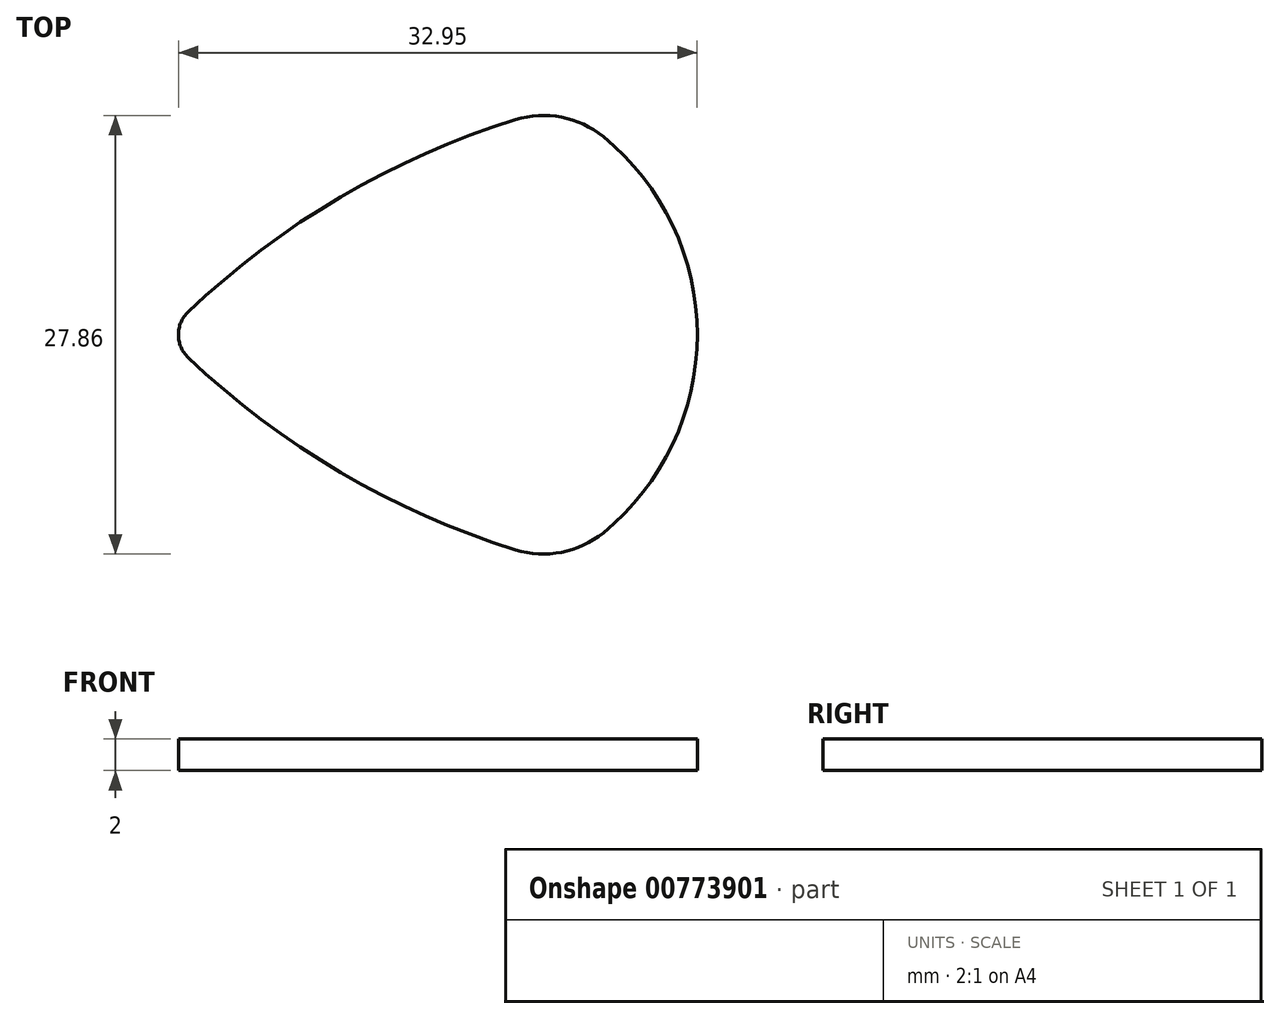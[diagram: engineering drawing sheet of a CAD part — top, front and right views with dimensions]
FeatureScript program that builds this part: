
annotation { "Feature Type Name" : "Feature", "Feature Type Description" : "" }
export const myFeature = defineFeature(function(context is Context, id is Id, definition is map)
    precondition{}
    {
        {
            var Q0;
            Q0=qCreatedBy(makeId("Top.planeOp"),FACE);
            var sketch = newSketch(context, id + "F0", { "sketchPlane" : qUnion([Q0])});
            skCircle(sketch, "E0.cCircle", {"center": v(0, 0) * mm, "radius": 8.33 * mm, "construction": true});
            skLineSegment(sketch, "E0.0", {"start": v(8.33, 14.43) * mm, "end": v(8.33, -14.43) * mm});
            skLineSegment(sketch, "E0.1", {"start": v(8.33, -14.43) * mm, "end": v(-16.67, 0) * mm});
            skLineSegment(sketch, "E0.2", {"start": v(-16.67, 0) * mm, "end": v(8.33, 14.43) * mm});
            skPoint(sketch, "E0.0.midPoint", {"position": v(8.33, 0) * mm});
            skPoint(sketch, "E1.visualSharp", {"position": v(-16.67, 0) * mm});
            skPoint(sketch, "E2.visualSharp", {"position": v(8.33, -14.43) * mm});
            skPoint(sketch, "E3.visualSharp", {"position": v(8.33, 14.43) * mm});
            skArc(sketch, "E4", {"start": v(-15.2, -1.45) * mm, "mid": v(-5.5, -8.75) * mm, "end": v(5.59, -13.66) * mm});
            skArc(sketch, "E5", {"start": v(5.59, 13.66) * mm, "mid": v(-5.5, 8.75) * mm, "end": v(-15.2, 1.45) * mm});
            skArc(sketch, "E6.filletArc", {"start": v(-15.2, 1.45) * mm, "mid": v(-15.82, 0) * mm, "end": v(-15.2, -1.45) * mm});
            skArc(sketch, "E7", {"start": v(11.16, -12.58) * mm, "mid": v(17.13, 0) * mm, "end": v(11.16, 12.58) * mm});
            skArc(sketch, "E8.filletArc", {"start": v(11.16, 12.58) * mm, "mid": v(8.51, 13.82) * mm, "end": v(5.59, 13.66) * mm});
            skArc(sketch, "E9.filletArc", {"start": v(5.59, -13.66) * mm, "mid": v(8.51, -13.82) * mm, "end": v(11.16, -12.58) * mm});
            skSolve(sketch);
        }
        {
            var Q0;
            {var subQ5=sQuery(id+"F0.wireOp",EDGE,"E7");Q0=makeQuery(id+"F0.imprint","IMPRINT",FACE,{"disambiguationData":[TD([[makeQuery(id+"F0.imprint","IMPRINT",EDGE,{"derivedFrom":subQ5}),1.0]])]});}
            var Q1;
            {var subQ5=sQuery(id+"F0.wireOp",EDGE,"E5");Q1=makeQuery(id+"F0.imprint","IMPRINT",FACE,{"disambiguationData":[TD([[makeQuery(id+"F0.imprint","IMPRINT",EDGE,{"derivedFrom":subQ5}),1.0]])]});}
            var Q2;
            {var subQ5=sQuery(id+"F0.wireOp",EDGE,"E8.filletArc");var subQ6=sQuery(id+"F0.wireOp",EDGE,"E0.0");var subQ7=makeQuery(id+"F0.imprint","INTERSECT",VERTEX,{"derivedFrom":[subQ6,subQ5]});Q2=makeQuery(id+"F0.imprint","IMPRINT",FACE,{"disambiguationData":[TD([[makeQuery(id+"F0.imprint","IMPRINT",EDGE,{"disambiguationData":[TD([[subQ7,-1.0]])],"derivedFrom":subQ6}),-1.0]])]});}
            var Q3;
            {var subQ5=sQuery(id+"F0.wireOp",EDGE,"E4");Q3=makeQuery(id+"F0.imprint","IMPRINT",FACE,{"disambiguationData":[TD([[makeQuery(id+"F0.imprint","IMPRINT",EDGE,{"derivedFrom":subQ5}),1.0]])]});}
            extrude(context, id + "F1", {"entities" : qUnion([Q0, Q1, Q2, Q3]), "depth" : 2 * mm, "offsetDistance" : 25 * mm});
        }
    });
